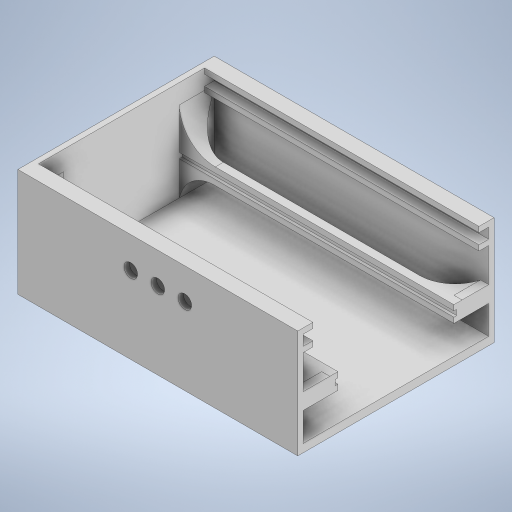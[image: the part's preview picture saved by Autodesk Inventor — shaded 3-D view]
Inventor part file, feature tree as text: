
AUTODESK INVENTOR PART (.ipt)
format: ipt  version: 2023 (Build 270158000, 158)  size: 378,880 bytes
history: native  units: mm
features: extrude x7, sketch x6, fillet x2
ambient origin geometry x8: Origin, YZ Plane, XZ Plane, XY Plane, X Axis, Y Axis, Z Axis, Center Point
bodies: Solide1 (feature_tree)
feature tree (15):
  sketch  "Esquisse1"
  extrude  "Extrusion1"  Depth=99.5mm
  extrude  "Extrusion2"  Depth=68.6mm
  extrude  "Extrusion3"  Depth=2.0mm
  extrude  "Extrusion4"  Depth=3.0mm TaperAngle=0.0deg
  extrude  "Extrusion5"  Depth=40.0mm TaperAngle=0.0deg
  fillet  "Congé1"  Radius=40.0mm
  extrude  "Extrusion6"  Depth=2.0mm
  fillet  "Congé2"  Radius=2.0mm
  extrude  "Extrusion7"  Depth=3.9mm
  sketch  "Esquisse2"
  sketch  "Esquisse3"
  sketch  "Esquisse4"
  sketch  "Esquisse5"
  sketch  "Esquisse6"
